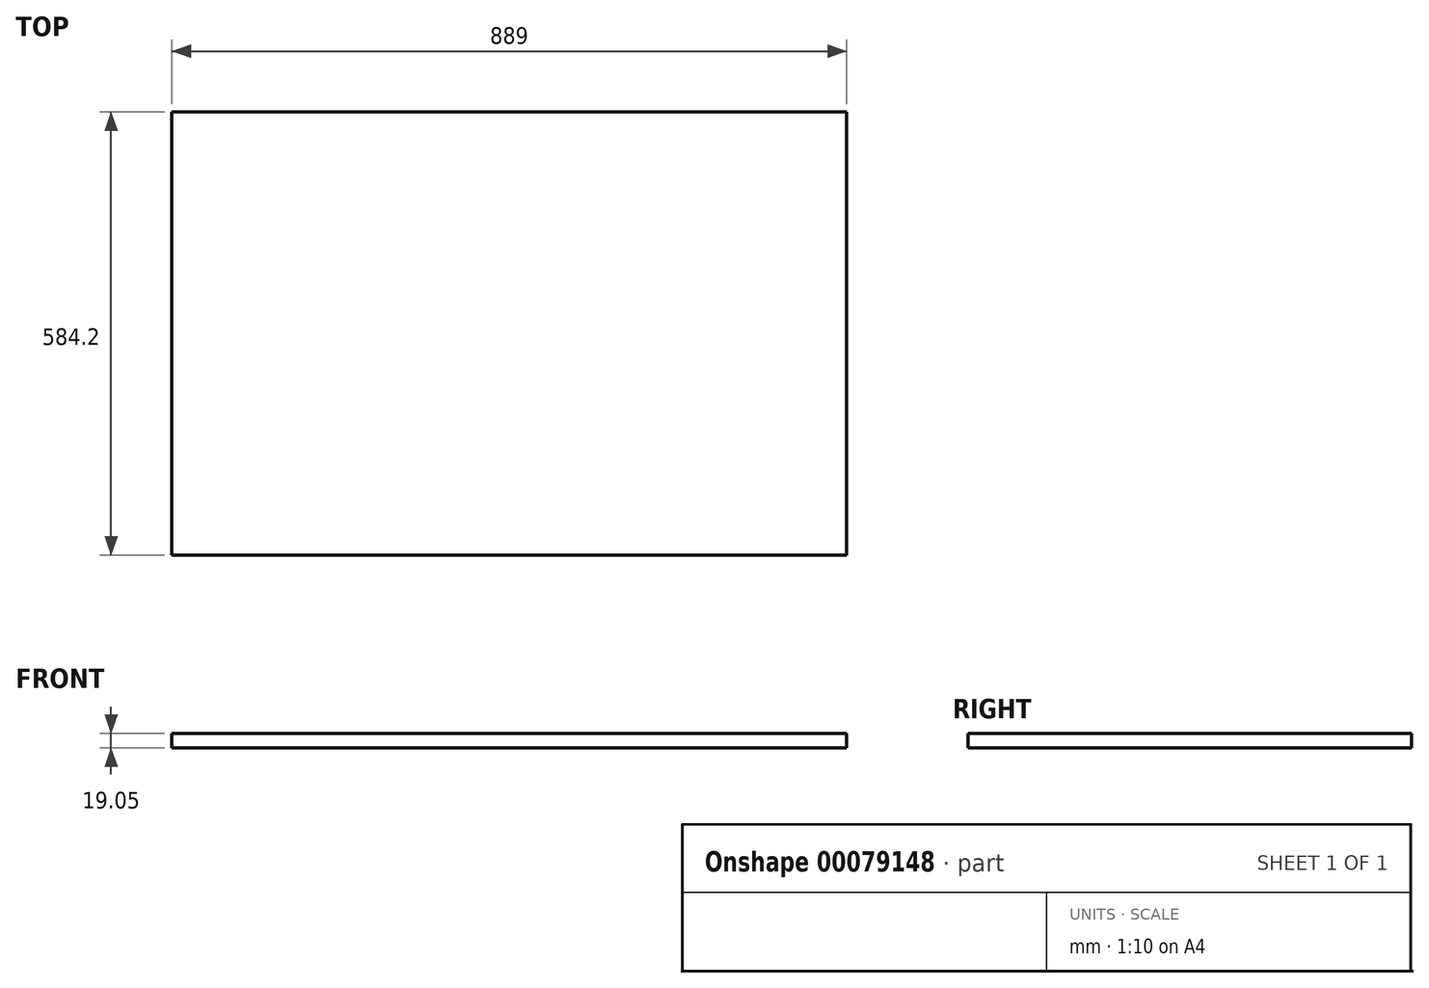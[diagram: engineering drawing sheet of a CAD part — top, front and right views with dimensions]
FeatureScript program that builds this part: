
annotation { "Feature Type Name" : "Feature", "Feature Type Description" : "" }
export const myFeature = defineFeature(function(context is Context, id is Id, definition is map)
    precondition{}
    {
        {
            var Q0;
            Q0=qCreatedBy(makeId("Top.planeOp"),FACE);
            var sketch = newSketch(context, id + "F0", { "sketchPlane" : qUnion([Q0])});
            skLineSegment(sketch, "E0.bottom", {"start": v(605.07, 369.07) * mm, "end": v(-283.93, 369.07) * mm});
            skLineSegment(sketch, "E0.top", {"start": v(605.07, -215.13) * mm, "end": v(-283.93, -215.13) * mm});
            skLineSegment(sketch, "E0.left", {"start": v(605.07, 369.07) * mm, "end": v(605.07, -215.13) * mm});
            skLineSegment(sketch, "E0.right", {"start": v(-283.93, 369.07) * mm, "end": v(-283.93, -215.13) * mm});
            skSolve(sketch);
        }
        {
            var Q0;
            Q0=makeQuery(id+"F0.imprint","IMPRINT",FACE,{"disambiguationData":[TD([[makeQuery(id+"F0.imprint","IMPRINT",EDGE,{"derivedFrom":sQuery(id+"F0.wireOp",EDGE,"E0.bottom")}),1.0]])]});
            extrude(context, id + "F1", {"entities" : qUnion([Q0]), "depth" : 19.05 * mm});
        }
    });
